# Revit family: STRT4X4-C128
name_source: partatom
category: Lighting Fixtures
units: mm (PartAtom-declared; Revit-internal decimal feet)

## family parameters
Always vertical = Yes
Cut with Voids When Loaded = No
Host = Ceiling
Light Source = Yes
Maintain Annotation Orientation = No
OmniClass Number = 23.80.70.11.14.17
OmniClass Title = Direct/Indirect
Part Type = Normal
Room Calculation Point = No
Round Connector Dimension = Use Diameter
Shared = No

## types (5) — shared parameters
Assembly Code = D5020200
Color Filter = 16777215
Default Elevation = 0' - 0"
Description = LED Fully Illuminated Backlit Premium Luminaire
Dimming Lamp Color Temperature Shift = <None>
Emit Shape Visible in Rendering = No
Emit from Rectangle Length = 3' - 11 3/4"
Emit from Rectangle Width = 3' - 11 3/4"
Height = 0' - 4"
Housing Finish = Metal - Viscor - White
Lamp = LED
Length = 3' - 11 3/4"
Lens Finish = Polycarbonate - Viscor - Frosted Round
Manufacturer = VISIONEERING by VISCOR
Model = STRT4X4-C128
Tilt Angle = 90.00°
URL = https://viscor.com
Voltage = 120 V
Width = 3' - 11 3/4"

## per-type parameters (varying)
| type | Apparent Load | Lamp Wattage | Photometric Web File |
| STRT4X4-LED840K080LUNV-C128 | 58 VA | 58 VA | STRT4x4-LED840K080LUNV-C128.ies |
| STRT4X4-LED840K100LUNV-C128 | 73 VA | 73 VA | STRT4x4-LED840K100LUNV-C128.ies |
| STRT4X4-LED840K120LUNV-C128 | 89 VA | 89 VA | STRT4x4-LED840K120LUNV-C128.ies |
| STRT4X4-LED840K140LUNV-C128 | 105 VA | 105 VA | STRT4x4-LED840K140LUNV-C128.ies |
| STRT4X4-LED840K160LUNV-C128 | 120 VA | 120 VA | STRT4x4-LED840K160LUNV-C128.ies |

## geometry (parser evidence)
native form markers: Sweep x3
no freeform markers — native parametric forms only
